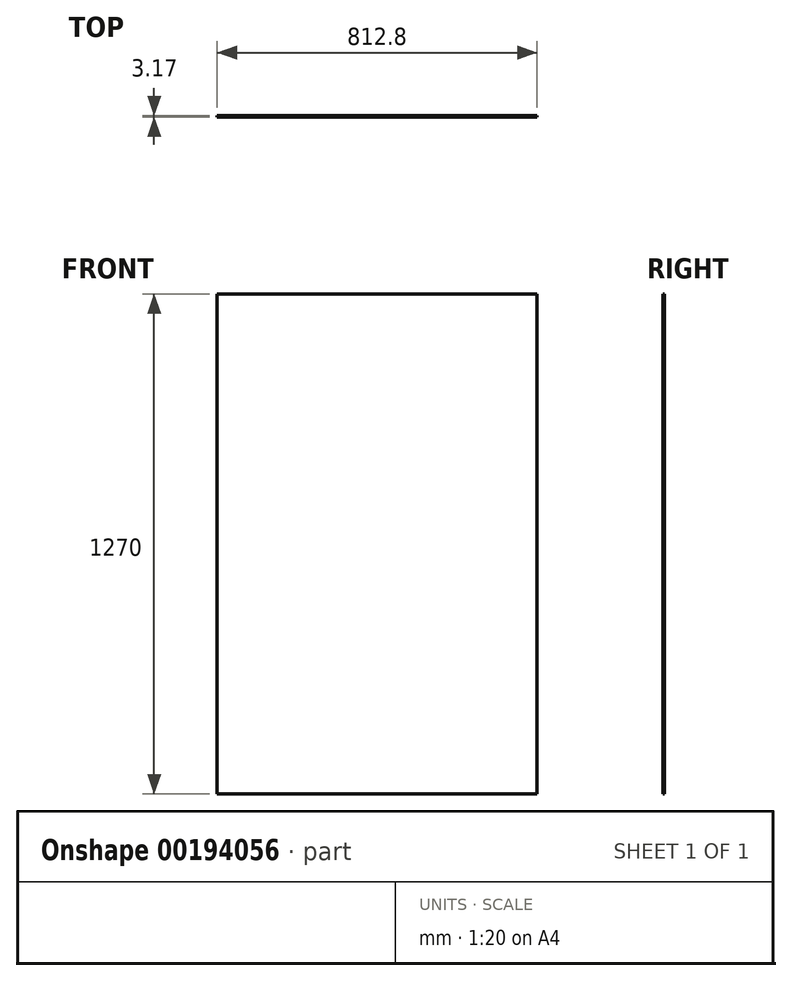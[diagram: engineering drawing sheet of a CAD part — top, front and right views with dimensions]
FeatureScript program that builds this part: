
annotation { "Feature Type Name" : "Feature", "Feature Type Description" : "" }
export const myFeature = defineFeature(function(context is Context, id is Id, definition is map)
    precondition{}
    {
        {
            var Q0;
            Q0=qCreatedBy(makeId("Front.planeOp"),FACE);
            var sketch = newSketch(context, id + "F0", { "sketchPlane" : qUnion([Q0])});
            skLineSegment(sketch, "E0.bottom", {"start": v(-406.4, 635) * mm, "end": v(406.4, 635) * mm});
            skLineSegment(sketch, "E0.top", {"start": v(-406.4, -635) * mm, "end": v(406.4, -635) * mm});
            skLineSegment(sketch, "E0.left", {"start": v(-406.4, 635) * mm, "end": v(-406.4, -635) * mm});
            skLineSegment(sketch, "E0.right", {"start": v(406.4, 635) * mm, "end": v(406.4, -635) * mm});
            skPoint(sketch, "E0.middle", {"position": v(0, 0) * mm});
            skSolve(sketch);
        }
        {
            var Q0;
            Q0=makeQuery(id+"F0.imprint","IMPRINT",FACE,{"disambiguationData":[TD([[makeQuery(id+"F0.imprint","IMPRINT",EDGE,{"derivedFrom":sQuery(id+"F0.wireOp",EDGE,"E0.bottom")}),-1.0]])]});
            extrude(context, id + "F1", {"entities" : qUnion([Q0]), "depth" : 3.17 * mm});
        }
    });
